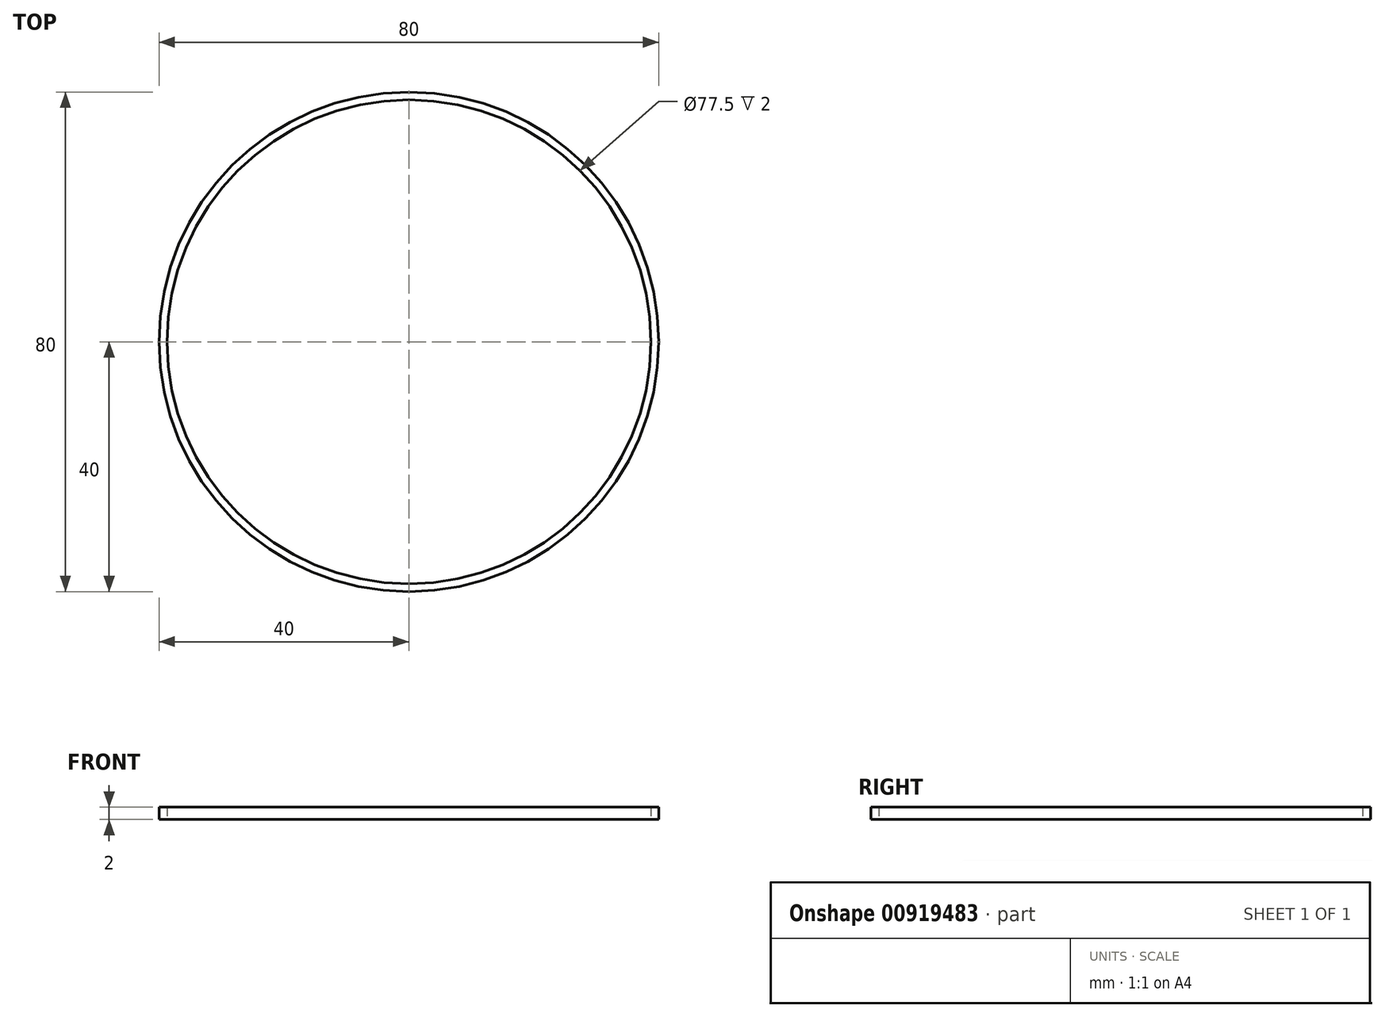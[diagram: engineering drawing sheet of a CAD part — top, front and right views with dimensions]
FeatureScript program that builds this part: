
annotation { "Feature Type Name" : "Feature", "Feature Type Description" : "" }
export const myFeature = defineFeature(function(context is Context, id is Id, definition is map)
    precondition{}
    {
        {
            var Q0;
            Q0=qCreatedBy(makeId("Top.planeOp"),FACE);
            var sketch = newSketch(context, id + "F0", { "sketchPlane" : qUnion([Q0])});
            skCircle(sketch, "E0", {"center": v(0, 0) * mm, "radius": 40 * mm});
            skCircle(sketch, "E1.0", {"center": v(0, 0) * mm, "radius": 38.75 * mm});
            skSolve(sketch);
        }
        {
            var Q0;
            Q0=qSketchRegion(id+"F0",true);
            extrude(context, id + "F1", {"entities" : qUnion([Q0]), "depth" : 2 * mm, "offsetDistance" : 25 * mm});
        }
    });
